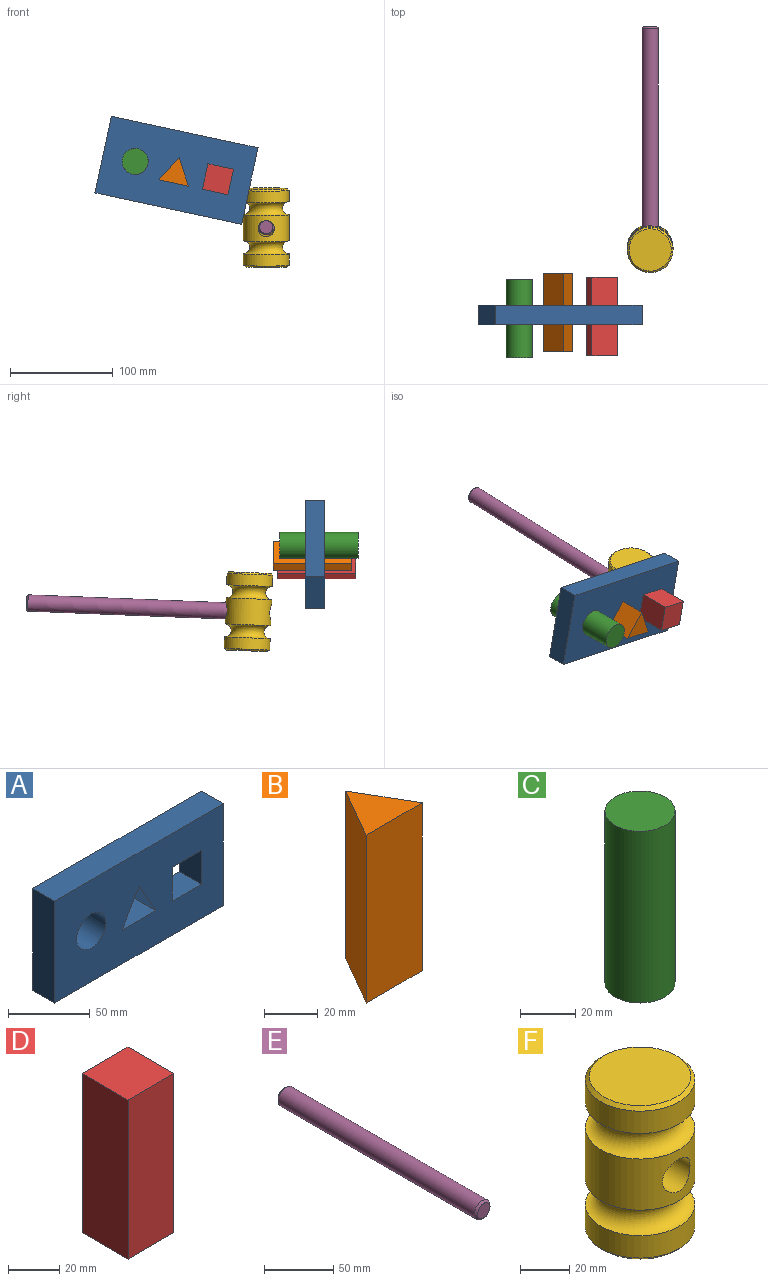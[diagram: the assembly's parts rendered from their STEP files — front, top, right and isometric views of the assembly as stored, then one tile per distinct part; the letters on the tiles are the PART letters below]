
ASSEMBLY  parts=6 mates=5
PART A: 14 faces, bbox 146.1x19.1x76.2 mm
  f0: plane 146.05x76.2mm, normal (0,-1,0), area 9604.7mm2, adj f2,f3,f4,f5,f6,f7,f8,f9
  f1: plane 146.05x76.2mm, normal (0,1,0), area 9604.7mm2, adj f2,f3,f4,f5,f6,f7,f8,f9
  f2: plane 76.2x19.05mm, normal (-1,0,0), area 1451.6mm2, adj f0,f1,f4,f5
  f3: plane 76.2x19.05mm, normal (1,0,0), area 1451.6mm2, adj f0,f1,f4,f5
  f4: plane 146.05x19.05mm, normal (0,0,1), area 2782.3mm2, adj f0,f1,f2,f3
  f5: plane 146.05x19.05mm, normal (0,0,-1), area 2782.3mm2, adj f0,f1,f2,f3
  f6: plane 25.4x19.05mm, normal (-0.87,0,-0.5), area 558.7mm2, adj f0,f1,f7,f8
  f7: plane 29.33x19.05mm, normal (0,0,1), area 558.7mm2, adj f0,f1,f6,f8
  f8: plane 25.4x19.05mm, normal (0.87,0,-0.5), area 558.7mm2, adj f0,f1,f6,f7
  f9: plane 25.4x19.05mm, normal (1,0,0), area 483.9mm2, adj f0,f1,f10,f12
  f10: plane 25.4x19.05mm, normal (0,0,-1), area 483.9mm2, adj f0,f1,f9,f11
  f11: plane 25.4x19.05mm, normal (-1,0,0), area 483.9mm2, adj f0,f1,f10,f12
  f12: plane 25.4x19.05mm, normal (0,0,1), area 483.9mm2, adj f0,f1,f9,f11
  f13: cylinder r=12.7mm len=25.4mm, axis (0,1,0), area 1520.1mm2, adj f0,f1
PART B: 5 faces, bbox 29.3x25.4x76.2 mm
  f0: plane 76.2x25.4mm, normal (-0.87,0.5,0), area 2234.9mm2, adj f1,f2,f3,f4
  f1: plane 76.2x29.33mm, normal (0,-1,0), area 2234.9mm2, adj f0,f2,f3,f4
  f2: plane 76.2x25.4mm, normal (0.87,0.5,0), area 2234.9mm2, adj f0,f1,f3,f4
  f3: plane 29.33x25.4mm, normal (0,0,1), area 372.5mm2, adj f0,f1,f2
  f4: plane 29.33x25.4mm, normal (0,0,-1), area 372.5mm2, adj f0,f1,f2
PART C: 3 faces, bbox 25.4x25.4x76.2 mm
  f0: cylinder r=12.7mm len=76.2mm, axis (0,0,-1), area 6080.5mm2, adj f1,f2
  f1: plane 25.4x25.4mm, normal (0,0,1), area 506.7mm2, adj f0
  f2: plane 25.4x25.4mm, normal (0,0,-1), area 506.7mm2, adj f0
PART D: 6 faces, bbox 25.4x25.4x76.2 mm
  f0: plane 76.2x25.4mm, normal (-1,0,0), area 1935.5mm2, adj f1,f3,f4,f5
  f1: plane 76.2x25.4mm, normal (0,-1,0), area 1935.5mm2, adj f0,f2,f4,f5
  f2: plane 76.2x25.4mm, normal (1,0,0), area 1935.5mm2, adj f1,f3,f4,f5
  f3: plane 76.2x25.4mm, normal (0,1,0), area 1935.5mm2, adj f0,f2,f4,f5
  f4: plane 25.4x25.4mm, normal (0,0,1), area 645.2mm2, adj f0,f1,f2,f3
  f5: plane 25.4x25.4mm, normal (0,0,-1), area 645.2mm2, adj f0,f1,f2,f3
PART E: 5 faces, bbox 15.9x203.2x15.9 mm
  f0: cylinder r=7.94mm len=200.03mm, axis (0,1,0), area 9975.8mm2, adj f3,f4
  f1: plane 12.7x12.7mm, normal (0,-1,0), area 126.7mm2, adj f4
  f2: plane 12.7x12.7mm, normal (0,1,0), area 126.7mm2, adj f3
  f3: cone r=7.94mm half-angle=45deg, axis (0,-1,0), area 100.8mm2, adj f0,f2
  f4: cone r=6.35mm half-angle=45deg, axis (0,1,0), area 100.8mm2, adj f0,f1
PART F: 10 faces, bbox 57.9x57.9x76.2 mm
  f0: plane 41.25x41.25mm, normal (0,0,-1), area 1336.4mm2, adj f7
  f1: cylinder r=22.23mm len=44.45mm, axis (0,0,1), area 1550mm2, adj f2,f7
  f2: torus R=22.23mm, axis (0,0,1), area 2279.1mm2, adj f1,f3
  f3: cylinder r=22.23mm len=44.45mm, axis (0,0,1), area 3145.1mm2, adj f2,f4,f9
  f4: torus R=22.23mm, axis (0,0,1), area 2279.1mm2, adj f3,f5
  f5: cylinder r=22.23mm len=44.45mm, axis (0,0,1), area 1550mm2, adj f4,f8
  f6: plane 41.25x41.25mm, normal (0,0,1), area 1336.4mm2, adj f8
  f7: cone r=22.23mm half-angle=45deg, axis (0,0,1), area 304.6mm2, adj f0,f1
  f8: cone r=20.62mm half-angle=45deg, axis (0,0,-1), area 304.6mm2, adj f5,f6
  f9: cylinder r=7.94mm len=44.45mm, axis (0,-1,0), area 2144.4mm2, adj f3
PLACE A rot(axis=(0,1,0),12.1deg) t=(-12.56,-11.71,3.41)mm
PLACE B rot(axis=(0.99,0.1,-0.1),90.6deg) t=(65.95,38.57,21.2)mm
PLACE C rot(axis=(-0.99,0.1,0.1),90.6deg) t=(26.48,-44.11,34)mm
PLACE D rot(axis=(-0.99,0.1,0.1),90.6deg) t=(96.9,-41.97,29.27)mm
PLACE E rot(axis=(1,0,0),2.3deg) t=(154.17,278.95,-21.97)mm
PLACE F rot(axis=(1,0,0),2.3deg) t=(154.17,61.11,7.51)mm
MATE slider D.f4 <-> A.f1  axis (0,1,0) through (107.19,34.23,16.68)mm
MATE slider B.f3 <-> A.f1  axis (0,-1,0) through (65.95,-37.63,21.2)mm
MATE slider C.f0 <-> A.f13  axis (0,-1,0) through (26.48,32.09,34)mm
MATE slider E.f0 <-> F.f9  axis (0,-1,-0.04) through (154.17,75.91,-30.04)mm
MATE slider B.f3 <-> A.f0  axis (0,-1,0) through (65.95,-37.63,21.2)mm
